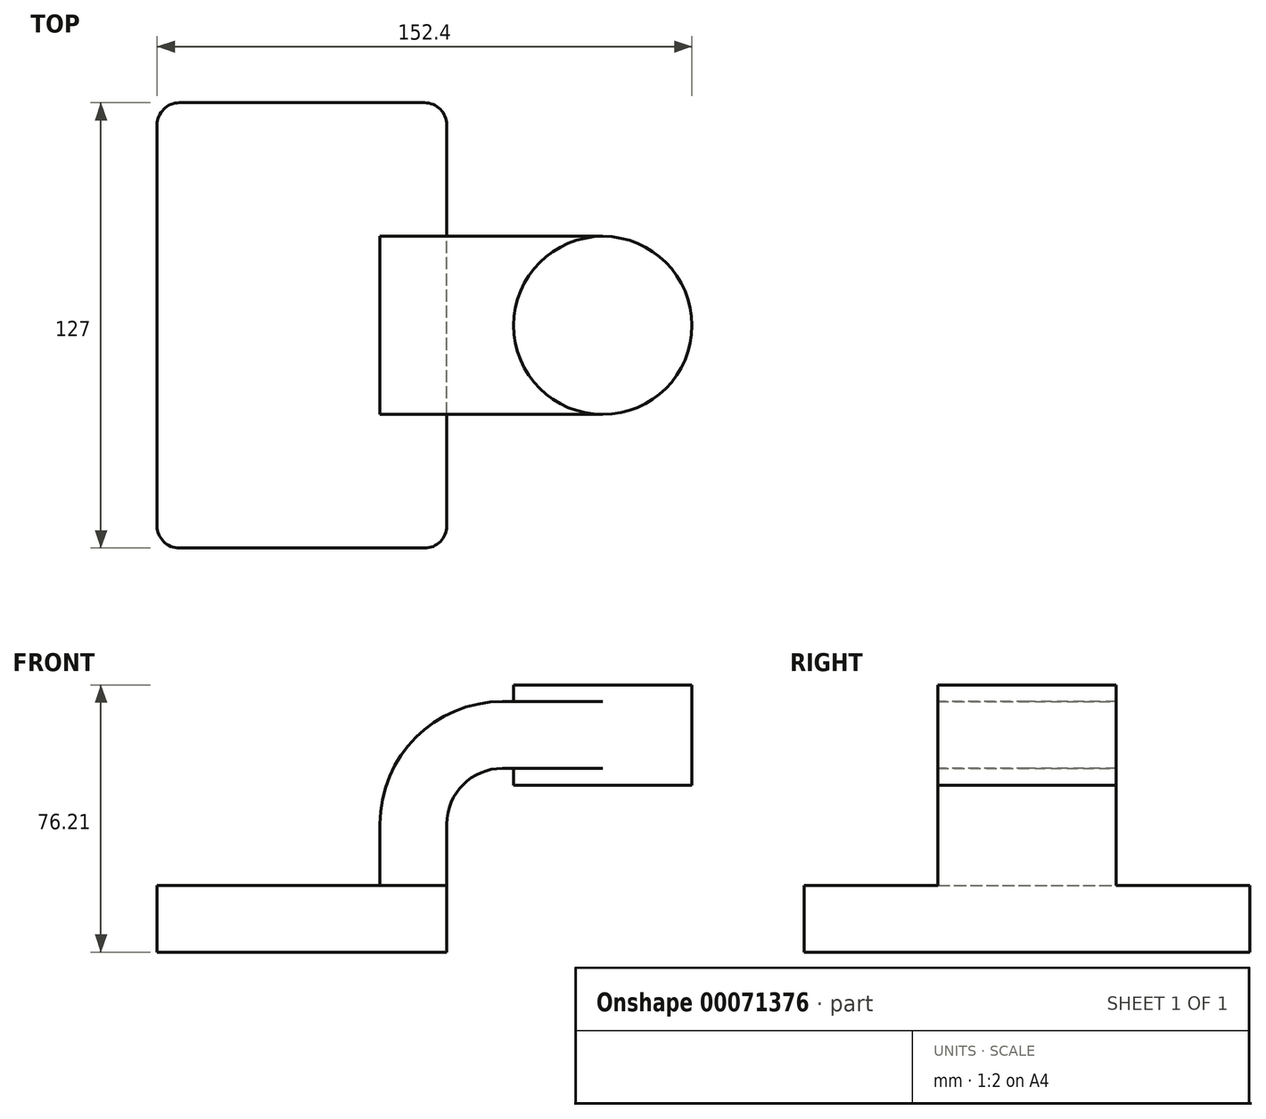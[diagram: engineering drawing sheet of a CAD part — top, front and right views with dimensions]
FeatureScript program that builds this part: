
annotation { "Feature Type Name" : "Feature", "Feature Type Description" : "" }
export const myFeature = defineFeature(function(context is Context, id is Id, definition is map)
    precondition{}
    {
        {
            var Q0;
            Q0=qCreatedBy(makeId("Front.planeOp"),FACE);
            var sketch = newSketch(context, id + "F0", { "sketchPlane" : qUnion([Q0])});
            skLineSegment(sketch, "E0.rect.bottom", {"start": v(41.27, 9.53) * mm, "end": v(-41.28, 9.53) * mm});
            skLineSegment(sketch, "E0.rect.top", {"start": v(41.28, -9.52) * mm, "end": v(-41.27, -9.52) * mm});
            skLineSegment(sketch, "E0.rect.left", {"start": v(41.28, 9.53) * mm, "end": v(41.28, -9.52) * mm});
            skLineSegment(sketch, "E0.rect.right", {"start": v(-41.28, 9.53) * mm, "end": v(-41.28, -9.52) * mm});
            skPoint(sketch, "E0.rect.middle", {"position": v(0, 0) * mm});
            skPoint(sketch, "E1.rect.middle", {"position": v(41.27, 9.53) * mm});
            skPoint(sketch, "E2.rect.middle", {"position": v(85.72, 52.39) * mm});
            skLineSegment(sketch, "E3.rect.bottom", {"start": v(111.12, 66.68) * mm, "end": v(60.32, 66.68) * mm});
            skLineSegment(sketch, "E3.rect.top", {"start": v(111.12, 38.1) * mm, "end": v(60.33, 38.1) * mm});
            skLineSegment(sketch, "E3.rect.left", {"start": v(111.12, 66.68) * mm, "end": v(111.12, 38.1) * mm});
            skLineSegment(sketch, "E3.rect.right", {"start": v(60.32, 66.68) * mm, "end": v(60.33, 38.1) * mm});
            skLineSegment(sketch, "E4", {"start": v(41.27, 9.53) * mm, "end": v(41.27, 27) * mm});
            skArc(sketch, "E5", {"start": v(41.27, 27) * mm, "mid": v(45.92, 38.23) * mm, "end": v(57.15, 42.88) * mm});
            skLineSegment(sketch, "E6", {"start": v(57.15, 42.88) * mm, "end": v(85.72, 42.88) * mm});
            skLineSegment(sketch, "E7.0", {"start": v(57.15, 61.93) * mm, "end": v(85.72, 61.93) * mm});
            skArc(sketch, "E7.1", {"start": v(22.22, 27) * mm, "mid": v(32.45, 51.7) * mm, "end": v(57.15, 61.93) * mm});
            skLineSegment(sketch, "E7.2", {"start": v(22.23, 9.53) * mm, "end": v(22.23, 27) * mm});
            skLineSegment(sketch, "E8", {"start": v(85.72, 38.1) * mm, "end": v(85.72, 66.68) * mm});
            skFitSpline(sketch, "E9", {"points": [v(-41.28, 9.53) * mm, v(57.15, 61.93) * mm], "startDerivative": vector(-4.27, 48.37) * mm, "endDerivative": vector(137.92, -12.38) * mm});
            skSolve(sketch);
        }
        {
            var Q0;
            Q0=makeQuery(id+"F0.imprint","IMPRINT",FACE,{"disambiguationData":[TD([[makeQuery(id+"F0.imprint","IMPRINT",EDGE,{"derivedFrom":sQuery(id+"F0.wireOp",EDGE,"E0.rect.top")}),-1.0]])]});
            extrude(context, id + "F1", {"entities" : qUnion([Q0]), "depth" : 127 * mm, "symmetric" : true});
        }
        {
            var Q0;
            {var subQ0=sQuery(id+"F0.wireOp",EDGE,"E7.0");var subQ1=sQuery(id+"F0.wireOp",EDGE,"E3.rect.right");var subQ2=makeQuery(id+"F0.imprint","INTERSECT",VERTEX,{"derivedFrom":[subQ1,subQ0]});Q0=makeQuery(id+"F0.imprint","IMPRINT",FACE,{"disambiguationData":[TD([[makeQuery(id+"F0.imprint","IMPRINT",EDGE,{"disambiguationData":[TD([[subQ2,-1.0]])],"derivedFrom":subQ1}),1.0]])]});}
            var Q1;
            {var subQ1=sQuery(id+"F0.wireOp",EDGE,"E4");Q1=makeQuery(id+"F0.imprint","IMPRINT",FACE,{"disambiguationData":[TD([[makeQuery(id+"F0.imprint","IMPRINT",EDGE,{"derivedFrom":subQ1}),1.0]])]});}
            extrude(context, id + "F2", {"entities" : qUnion([Q0, Q1]), "operationType" : NewBodyOperationType.ADD, "depth" : 50.8 * mm, "symmetric" : true});
        }
        {
            var Q0;
            Q0=makeQuery(id+"F0.imprint","IMPRINT",FACE,{"disambiguationData":[TD([[makeQuery(id+"F0.imprint","IMPRINT",EDGE,{"derivedFrom":sQuery(id+"F0.wireOp",EDGE,"E7.1")}),1.0]])]});
            extrude(context, id + "F3", {"entities" : qUnion([Q0]), "operationType" : NewBodyOperationType.ADD, "depth" : 15.88 * mm, "symmetric" : true});
        }
        {
            var Q0;
            {var subQ0=sQuery(id+"F0.wireOp",EDGE,"E3.rect.left");Q0=makeQuery(id+"F0.imprint","IMPRINT",FACE,{"disambiguationData":[TD([[makeQuery(id+"F0.imprint","IMPRINT",EDGE,{"derivedFrom":subQ0}),-1.0]])]});}
            var Q1;
            Q1=sQuery(id+"F0.wireOp",EDGE,"E8");
            revolve(context, id + "F4", {"operationType" : NewBodyOperationType.ADD, "entities" : qUnion([Q0]), "axis" : qUnion([Q1]), "revolveType" : RevolveType.FULL});
        }
        {
            var Q0;
            Q0=makeQuery(id+"F1.opExtrude","CAP_EDGE",EDGE,{"disambiguationData":[OSD([sQuery(id+"F0.wireOp",EDGE,"E0.rect.left")])],"isStart":false});
            var Q1;
            Q1=makeQuery(id+"F1.opExtrude","CAP_EDGE",EDGE,{"disambiguationData":[OSD([sQuery(id+"F0.wireOp",EDGE,"E0.rect.right")])],"isStart":false});
            var Q2;
            Q2=makeQuery(id+"F1.opExtrude","CAP_EDGE",EDGE,{"disambiguationData":[OSD([sQuery(id+"F0.wireOp",EDGE,"E0.rect.left")])],"isStart":true});
            var Q3;
            Q3=makeQuery(id+"F1.opExtrude","CAP_EDGE",EDGE,{"disambiguationData":[OSD([sQuery(id+"F0.wireOp",EDGE,"E0.rect.right")])],"isStart":true});
            fillet(context, id + "F5", {"entities" : qUnion([Q0, Q1, Q2, Q3]), "radius" : 6.35 * mm, "tangentPropagation" : true, "allowEdgeOverflow" : false});
        }
    });
